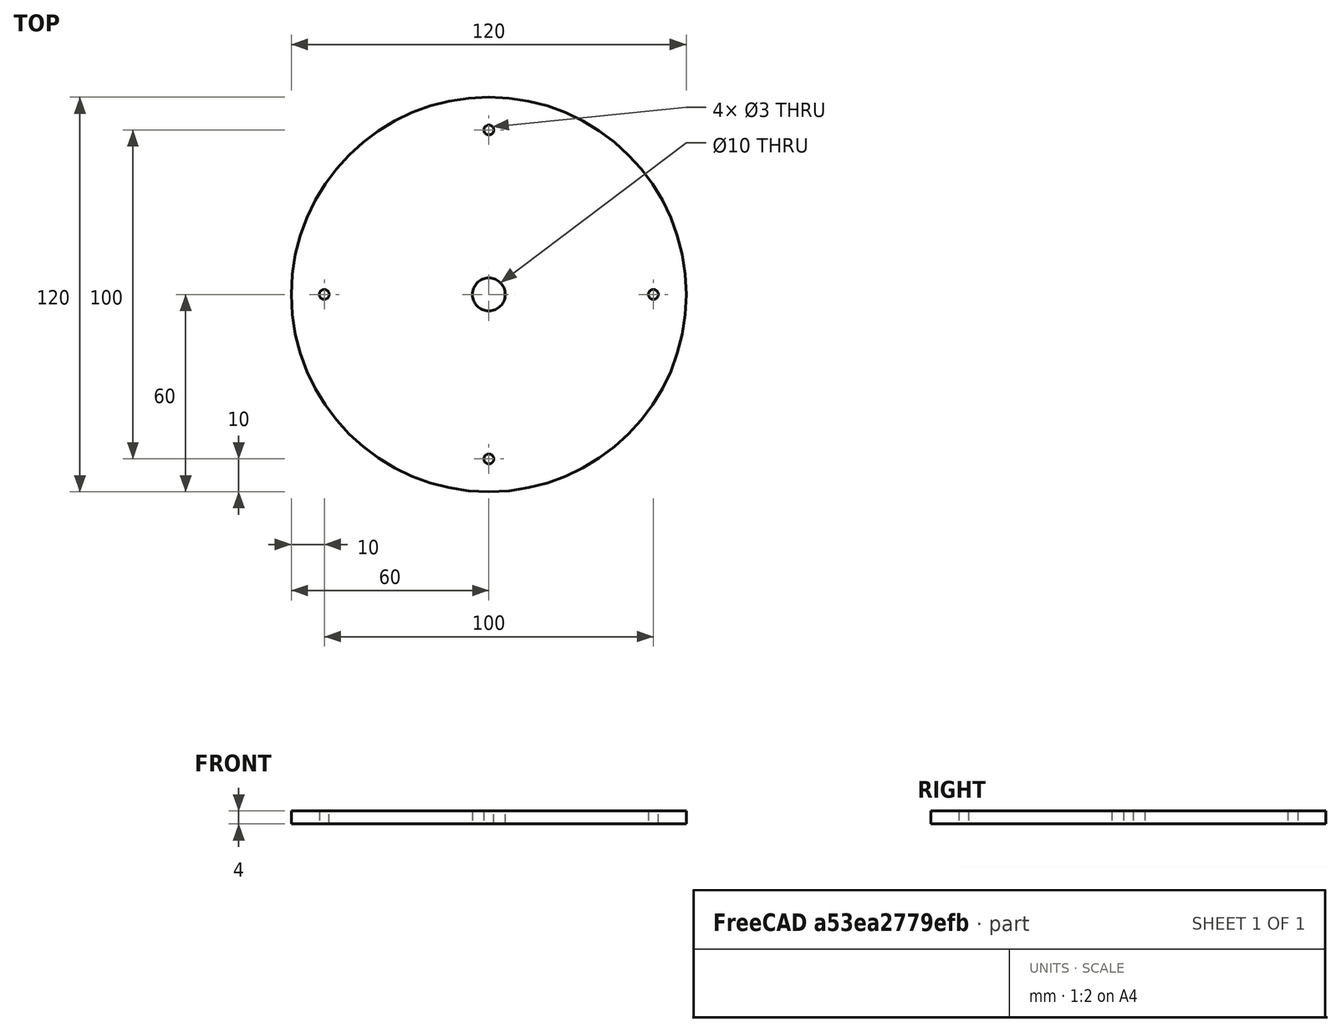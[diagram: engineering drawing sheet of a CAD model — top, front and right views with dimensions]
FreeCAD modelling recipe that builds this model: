
FCSTD DOCUMENT  (FreeCAD 0.19R24276 (Git))
Label: circle_seal_holder_part2_d10
License: All rights reserved
LicenseURL: http://en.wikipedia.org/wiki/All_rights_reserved
objects: Sketcher::SketchObject×1, PartDesign::Pad×1, PartDesign::Body×1
note: 4 computed .brp shape members not serialized (recipe doc carries the construction recipe); baked Part::Feature solids carry a one-line shape summary decoded from their .brp

FEATURE [Sketcher::SketchObject] Sketch
  FullyConstrained = true
  MapMode = 5
  Support = -> [XY_Plane]
  sketch-geometry (11):
    g0: Circle CenterX=0 CenterY=0 CenterZ=0 NormalX=0 NormalY=0 NormalZ=1 AngleXU=0 Radius=5
    g1: Circle CenterX=0 CenterY=0 CenterZ=0 NormalX=0 NormalY=0 NormalZ=1 AngleXU=0 Radius=60
    g2: Circle CenterX=0 CenterY=50 CenterZ=0 NormalX=0 NormalY=0 NormalZ=1 AngleXU=0 Radius=1.5
    g3: Circle CenterX=0 CenterY=-50 CenterZ=0 NormalX=0 NormalY=0 NormalZ=1 AngleXU=0 Radius=1.5
    g4: Circle CenterX=50 CenterY=0 CenterZ=0 NormalX=0 NormalY=0 NormalZ=1 AngleXU=0 Radius=1.5
    g5: Circle CenterX=-50 CenterY=0 CenterZ=0 NormalX=0 NormalY=0 NormalZ=1 AngleXU=0 Radius=1.5
    g6: Circle CenterX=0 CenterY=0 CenterZ=0 NormalX=0 NormalY=0 NormalZ=1 AngleXU=0 Radius=50
    g7: LineSegment StartX=0 StartY=0 StartZ=0 EndX=-50 EndY=0 EndZ=0
    g8: LineSegment StartX=0 StartY=0 StartZ=0 EndX=0 EndY=50 EndZ=0
    g9: LineSegment StartX=0 StartY=0 StartZ=0 EndX=50 EndY=0 EndZ=0
    g10: LineSegment StartX=0 StartY=0 StartZ=0 EndX=0 EndY=-50 EndZ=0
  constraints (26):
    c: Coincident(g0,g-1)
    c: Diameter(g0) = 10
    c: Coincident(g1,g0)
    c: Diameter(g1) = 120
    c: PointOnObject(g2,g-2)
    c: PointOnObject(g3,g-2)
    c: PointOnObject(g4,g-1)
    c: PointOnObject(g5,g-1)
    c: Diameter(g2) = 3
    c: Equal(g2,g5)
    c: Equal(g2,g3)
    c: Equal(g2,g4)
    c: Coincident(g6,g0)
    c: Coincident(g7,g0)
    c: Coincident(g8,g0)
    c: Coincident(g9,g0)
    c: Coincident(g10,g0)
    c: PointOnObject(g10,g6)
    c: PointOnObject(g7,g6)
    c: PointOnObject(g8,g6)
    c: PointOnObject(g9,g6)
    c: Coincident(g5,g7)
    c: Coincident(g2,g8)
    c: Coincident(g4,g9)
    c: Coincident(g3,g10)
    c: Diameter(g6) = 100  '1'
FEATURE [PartDesign::Pad] Pad
  Direction = (1,1,1)
  Length = 4
  Length2 = 100
  Profile = -> Sketch
  Type = 0
FEATURE [PartDesign::Body] Body
  Group = -> [Sketch,Pad]
  Origin = -> Origin
  Tip = -> Pad
